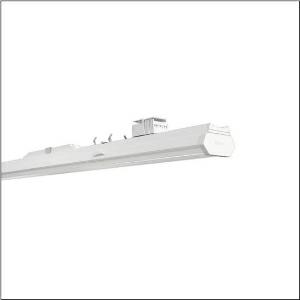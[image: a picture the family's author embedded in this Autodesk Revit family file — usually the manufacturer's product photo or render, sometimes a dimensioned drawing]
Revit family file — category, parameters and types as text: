
# Revit family: licross_11_protected_mo_51tp127n485g
name_source: partatom
category: Lighting Fixtures
units: mm (PartAtom-declared; Revit-internal decimal feet)

## family parameters
Cut with Voids When Loaded = No
Host = Face
Light Source = No
Part Type = Normal
Room Calculation Point = No
Round Connector Dimension = Use Diameter
Shared = No

## types (1)
- Licross 11 Protected MO (1 x LED, 8720 lm, 48.6 W, 4000K)
    Apparent Load = 49 VA
    CIE Flux Codes = 73 92 98 99 100
    Color Rendering = 80
    Color Temperature = 4000K
    Default Elevation = 1800 mm
    Description = Licross 11 Protected MO, luminaire insert, of sheet steel, galvanised, coil coated, white, length: 1.500mm, width: 90mm, height: 101mm, LED rated luminous flux: 8.720lm, light colour: 840, SDCM (Standard Deviation of Colour Matching)MacAdam ≤ 2 SDCM (initial), control gear: ON/OFF, with plug, 3-pole, with phase selection, mains connection: 220..240V, AC, 50/60Hz, rated input power: 49W, internal wiring halogen-free, primary light control with lens, of plastic, primary optical cover: cover, of PMMA, light emission: direct distribution, primary light characteristic: symmetric, protection rating (complete): IP64, insulation class (complete): insulation class I (protective earthing), certification: CE, ENEC, VDE, UKCA, protection symbol: D if used in an environment with conductive dust loads with corresponding accessories, impact resistance: IK06, permissible ambient temperature for indoor applications: -25..+35°C, corresponds to IFS (International Featured Standards) requirements for safety and quality in the food industry, reducing of maximum allowable ambient temperature of 5°C with ceiling mounting, LABS conformity tested according to VDMA 24364:2018-05, The light source and the operating device comply with the requirements of the Ecodesign Regulation (EU) 2019/2020 and are replaceable in accordance with this regulation, packaging unit: 1 piece
    Height = 92 mm
    Lamp = 1 x LED
    Lamp Light Flux = 8720 lm
    Lamp Power = 48.6 W
    Lamp count = 1
    Length = 1500 mm
    Luminous efficacy = 179 lm/W
    Manufacturer = Siteco
    ModVariant = No
    Model = 51TP127N485G
    Mounting Place = Ceiling
    Mounting Type = Pendant
    Number of Poles = 1
    OnlyDefault = Yes
    Power Factor = 1
    Product Name = Licross 11 Protected MO
    Product group = luminaire insert | ceiling pendant
    ProductGroupID = 901
    Protection Class = Protection class I
    Protection Degree = IP 64
    RLX_Detail_Level = 1
    RLX_Emergency_Light_Flux = 0 lm
    RLX_Emergency_Type = 0
    RLX_Emergency_Type_DB = No
    RlxData = <blob elided: 21009 chars, md5=76981679>
    Socket = socket
    Standby Power = 0 W
    System Light Flux = 8720 lm
    System Power = 49 W
    Type Comments = Product without accessories
    Type Image = l_1256148.jpg
    URL = http://relux.com
    VarID = ---
    Voltage = 0 V
    Weight = 0.00 kg
    Width = 88 mm

## geometry (parser evidence)
native form markers: Blend x4, Sweep x12
no freeform markers — native parametric forms only
